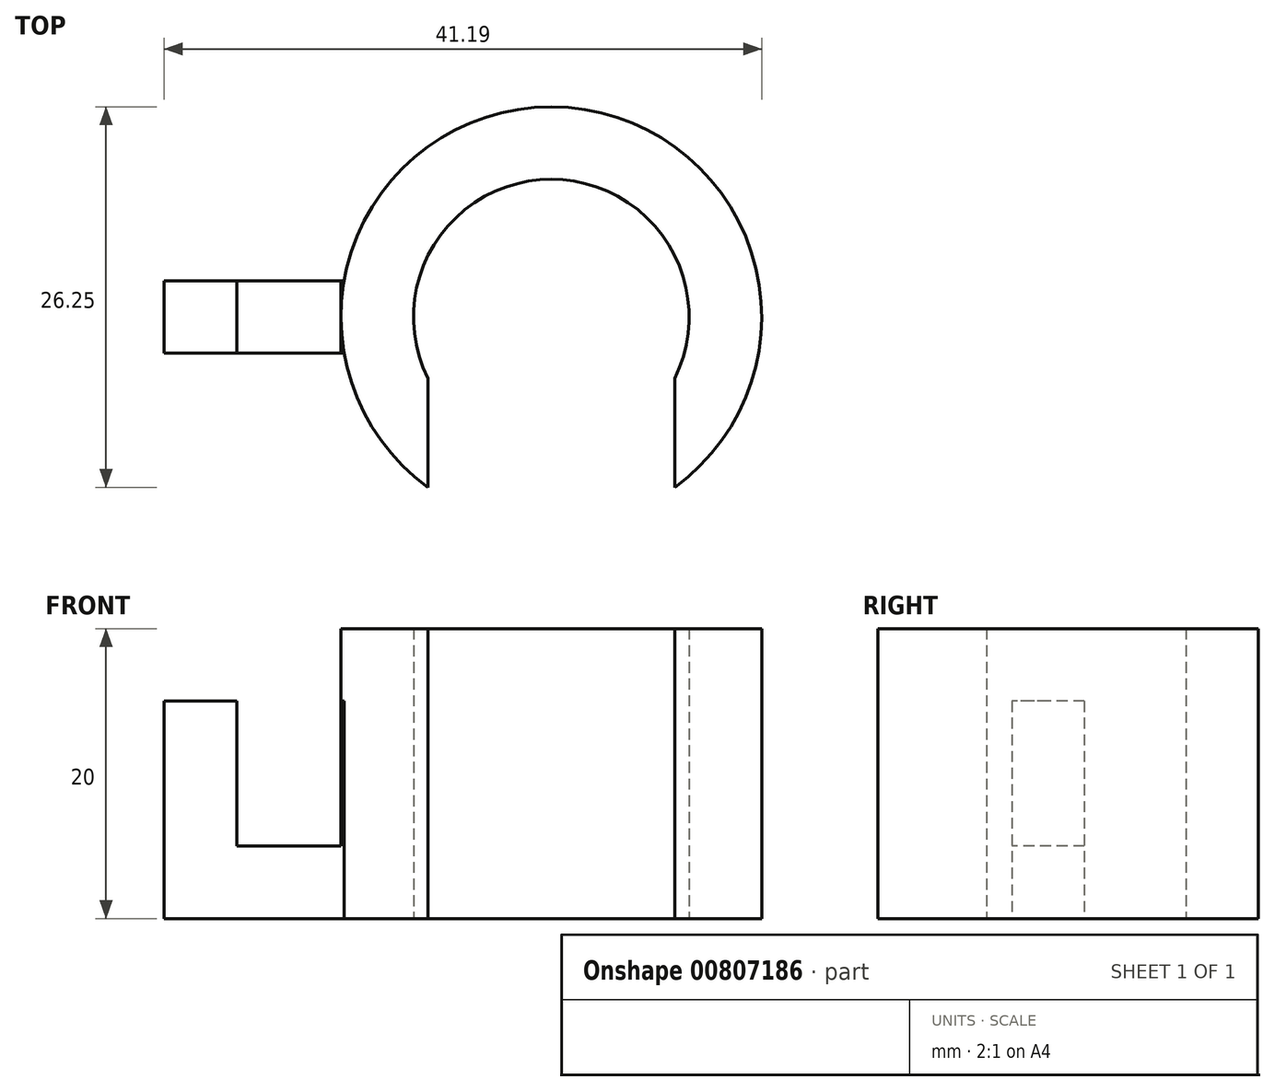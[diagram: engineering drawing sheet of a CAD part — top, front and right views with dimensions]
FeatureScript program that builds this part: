
annotation { "Feature Type Name" : "Feature", "Feature Type Description" : "" }
export const myFeature = defineFeature(function(context is Context, id is Id, definition is map)
    precondition{}
    {
        {
            var Q0;
            Q0=qCreatedBy(makeId("Top.planeOp"),FACE);
            var sketch = newSketch(context, id + "F0", { "sketchPlane" : qUnion([Q0])});
            skCircle(sketch, "E0", {"center": v(0, 0) * mm, "radius": 9.5 * mm});
            skCircle(sketch, "E1", {"center": v(0, 0) * mm, "radius": 14.5 * mm});
            skSolve(sketch);
        }
        {
            var Q0;
            Q0=makeQuery(id+"F0.imprint","IMPRINT",FACE,{"disambiguationData":[TD([[makeQuery(id+"F0.imprint","IMPRINT",EDGE,{"derivedFrom":sQuery(id+"F0.wireOp",EDGE,"E0")}),-1.0]])]});
            extrude(context, id + "F1", {"entities" : qUnion([Q0]), "depth" : 20 * mm, "offsetDistance" : 25 * mm});
        }
        {
            var Q0;
            Q0=qCreatedBy(makeId("Top.planeOp"),FACE);
            var sketch = newSketch(context, id + "F2", { "sketchPlane" : qUnion([Q0])});
            skLineSegment(sketch, "E2", {"start": v(-8.5, -20.35) * mm, "end": v(-8.5, 0) * mm});
            skLineSegment(sketch, "E3.MirrorCS", {"start": v(8.5, -20.35) * mm, "end": v(8.5, 0) * mm});
            skLineSegment(sketch, "E4", {"start": v(-8.5, -20.35) * mm, "end": v(8.5, -20.35) * mm});
            skLineSegment(sketch, "E5", {"start": v(-8.5, 0) * mm, "end": v(8.5, 0) * mm});
            skSolve(sketch);
        }
        {
            var Q0;
            Q0=makeQuery(id+"F2.imprint","IMPRINT",FACE,{"disambiguationData":[TD([[makeQuery(id+"F2.imprint","IMPRINT",EDGE,{"derivedFrom":sQuery(id+"F2.wireOp",EDGE,"E2")}),-1.0]])]});
            extrude(context, id + "F3", {"entities" : qUnion([Q0]), "operationType" : NewBodyOperationType.REMOVE, "depth" : 20 * mm, "offsetDistance" : 25 * mm});
        }
        {
            var Q0;
            Q0=makeQuery(id+"F1.opExtrude","CAP_FACE",FACE,{"disambiguationData":[OSD([sQuery(id+"F0.wireOp",EDGE,"E0"),sQuery(id+"F0.wireOp",EDGE,"E1")])],"isStart":true});
            var sketch = newSketch(context, id + "F4", { "sketchPlane" : qUnion([Q0])});
            skLineSegment(sketch, "E6", {"start": v(-14.28, 2.5) * mm, "end": v(-26.7, 2.5) * mm});
            skLineSegment(sketch, "E7.MirrorCS", {"start": v(-14.28, -2.5) * mm, "end": v(-26.7, -2.5) * mm});
            skLineSegment(sketch, "E8", {"start": v(-26.7, 2.5) * mm, "end": v(-26.7, -2.5) * mm});
            skSolve(sketch);
        }
        {
            var Q0;
            {var subQ0=sQuery(id+"F4.wireOp",EDGE,"E6");Q0=makeQuery(id+"F4.imprint","IMPRINT",FACE,{"disambiguationData":[TD([[makeQuery(id+"F4.imprint","IMPRINT",EDGE,{"derivedFrom":subQ0}),1.0]])]});}
            extrude(context, id + "F5", {"entities" : qUnion([Q0]), "operationType" : NewBodyOperationType.ADD, "oppositeDirection" : true, "depth" : 15 * mm, "offsetDistance" : 25 * mm});
        }
        {
            var Q0;
            Q0=makeQuery(id+"F5.opExtrude","SWEPT_FACE",FACE,{"disambiguationData":[OSD([sQuery(id+"F4.wireOp",EDGE,"E6")])]});
            var sketch = newSketch(context, id + "F6", { "sketchPlane" : qUnion([Q0])});
            skLineSegment(sketch, "E9", {"start": v(-14.5, 15) * mm, "end": v(-14.5, 20) * mm});
            skLineSegment(sketch, "E10", {"start": v(-14.5, 15) * mm, "end": v(-14.5, 5) * mm});
            skLineSegment(sketch, "E11", {"start": v(-14.5, 5) * mm, "end": v(-21.7, 5) * mm});
            skLineSegment(sketch, "E12", {"start": v(-21.7, 5) * mm, "end": v(-21.7, 15) * mm});
            skSolve(sketch);
        }
        {
            var Q0;
            {var subQ0=sQuery(id+"F6.wireOp",EDGE,"E10");Q0=makeQuery(id+"F6.imprint","IMPRINT",FACE,{"disambiguationData":[TD([[makeQuery(id+"F6.imprint","IMPRINT",EDGE,{"derivedFrom":subQ0}),-1.0]])]});}
            extrude(context, id + "F7", {"entities" : qUnion([Q0]), "operationType" : NewBodyOperationType.REMOVE, "oppositeDirection" : true, "depth" : 5 * mm, "offsetDistance" : 25 * mm});
        }
    });
